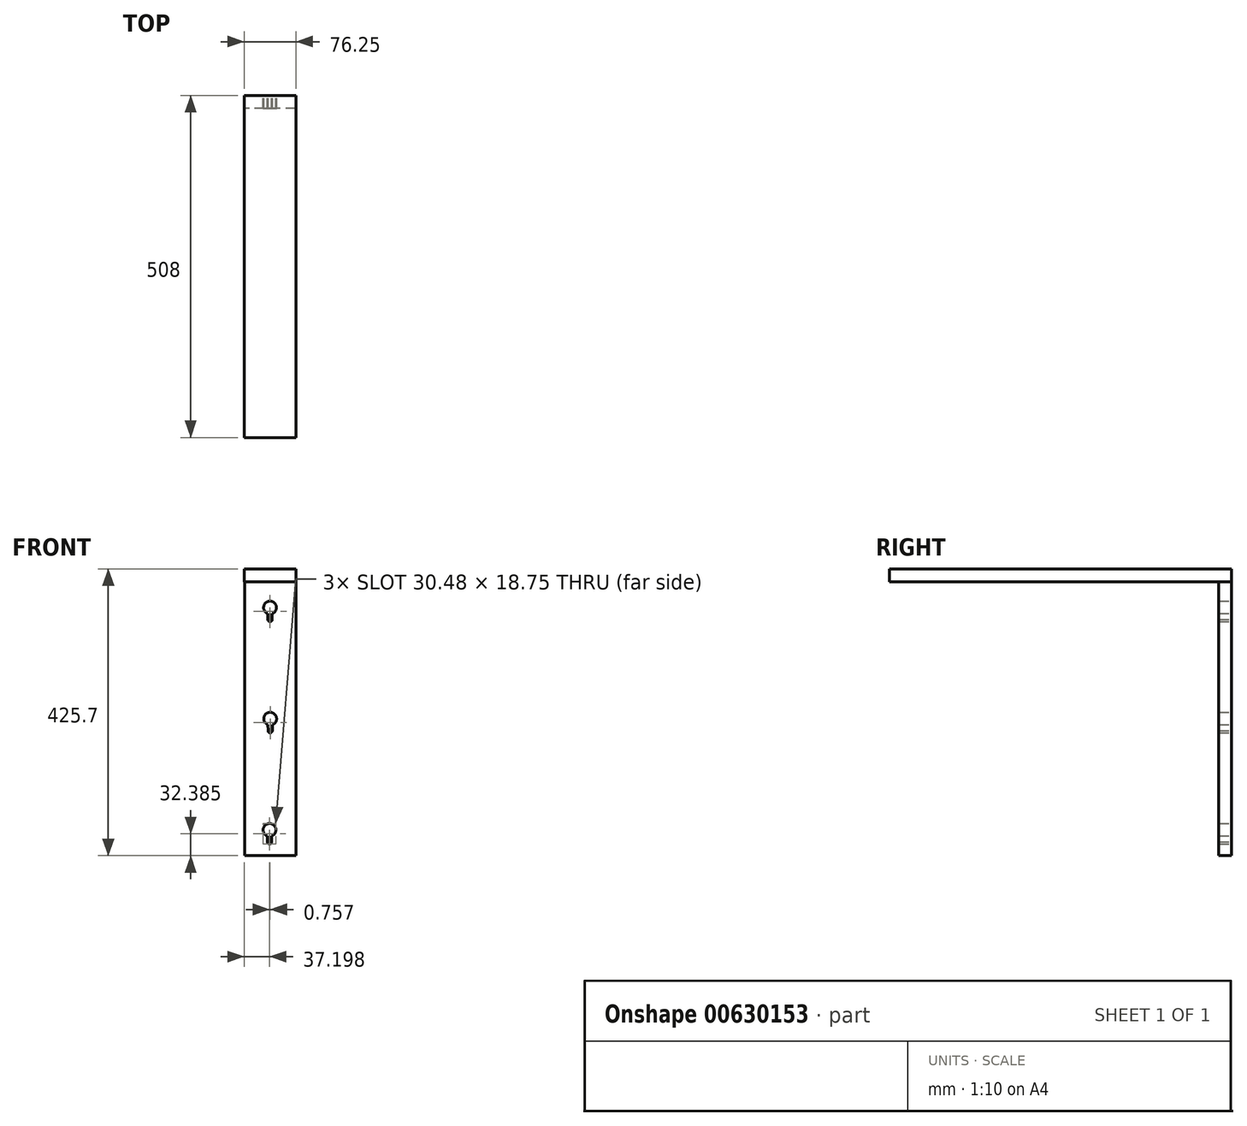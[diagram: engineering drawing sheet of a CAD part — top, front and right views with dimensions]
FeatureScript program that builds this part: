
annotation { "Feature Type Name" : "Feature", "Feature Type Description" : "" }
export const myFeature = defineFeature(function(context is Context, id is Id, definition is map)
    precondition{}
    {
        {
            var Q0;
            Q0=qCreatedBy(makeId("Front.planeOp"),FACE);
            var sketch = newSketch(context, id + "F0", { "sketchPlane" : qUnion([Q0])});
            skLineSegment(sketch, "E0.bottom", {"start": v(38.1, -203.2) * mm, "end": v(-38.1, -203.2) * mm});
            skLineSegment(sketch, "E0.top", {"start": v(38.1, 203.2) * mm, "end": v(-38.1, 203.2) * mm});
            skLineSegment(sketch, "E0.left", {"start": v(38.1, -203.2) * mm, "end": v(38.1, 203.2) * mm});
            skLineSegment(sketch, "E0.right", {"start": v(-38.1, -203.2) * mm, "end": v(-38.1, 203.2) * mm});
            skPoint(sketch, "E0.middle", {"position": v(0, 0) * mm});
            skCircle(sketch, "E1", {"center": v(0, 0) * mm, "radius": 9.53 * mm});
            skCircle(sketch, "E2", {"center": v(0, -17.78) * mm, "radius": 3.18 * mm});
            skLineSegment(sketch, "E3", {"start": v(-3.17, -17.99) * mm, "end": v(-3.41, -8.9) * mm});
            skLineSegment(sketch, "E4", {"start": v(3.18, -17.72) * mm, "end": v(3.18, -8.98) * mm});
            skCircle(sketch, "E5", {"center": v(-0.22, 165.1) * mm, "radius": 9.53 * mm});
            skCircle(sketch, "E6", {"center": v(-0.22, 147.32) * mm, "radius": 3.18 * mm});
            skLineSegment(sketch, "E7", {"start": v(-3.38, 147.11) * mm, "end": v(-3.63, 156.2) * mm});
            skLineSegment(sketch, "E8", {"start": v(2.96, 147.38) * mm, "end": v(2.96, 156.12) * mm});
            skCircle(sketch, "E9", {"center": v(-0.97, -165.1) * mm, "radius": 9.53 * mm});
            skCircle(sketch, "E10", {"center": v(-0.97, -182.88) * mm, "radius": 3.18 * mm});
            skLineSegment(sketch, "E11", {"start": v(-4.14, -183.09) * mm, "end": v(-4.39, -174) * mm});
            skLineSegment(sketch, "E12", {"start": v(2.2, -182.82) * mm, "end": v(2.2, -174.08) * mm});
            skSolve(sketch);
        }
        {
            var Q0;
            Q0=makeQuery(id+"F0.imprint","IMPRINT",FACE,{"disambiguationData":[TD([[makeQuery(id+"F0.imprint","IMPRINT",EDGE,{"derivedFrom":sQuery(id+"F0.wireOp",EDGE,"E0.bottom")}),-1.0]])]});
            extrude(context, id + "F1", {"entities" : qUnion([Q0]), "depth" : 19.05 * mm, "offsetDistance" : 25.4 * mm});
        }
        {
            var Q0;
            Q0=qCreatedBy(makeId("Front.planeOp"),FACE);
            var sketch = newSketch(context, id + "F2", { "sketchPlane" : qUnion([Q0])});
            skLineSegment(sketch, "E13.bottom", {"start": v(-38.15, 203.45) * mm, "end": v(38.05, 203.45) * mm});
            skLineSegment(sketch, "E13.top", {"start": v(-38.15, 222.5) * mm, "end": v(38.05, 222.5) * mm});
            skLineSegment(sketch, "E13.left", {"start": v(-38.15, 203.45) * mm, "end": v(-38.15, 222.5) * mm});
            skLineSegment(sketch, "E13.right", {"start": v(38.05, 203.45) * mm, "end": v(38.05, 222.5) * mm});
            skSolve(sketch);
        }
        {
            var Q0;
            Q0=makeQuery(id+"F2.imprint","IMPRINT",FACE,{"disambiguationData":[TD([[makeQuery(id+"F2.imprint","IMPRINT",EDGE,{"derivedFrom":sQuery(id+"F2.wireOp",EDGE,"E13.bottom")}),1.0]])]});
            extrude(context, id + "F3", {"entities" : qUnion([Q0]), "depth" : 508 * mm, "offsetDistance" : 25.4 * mm});
        }
    });
